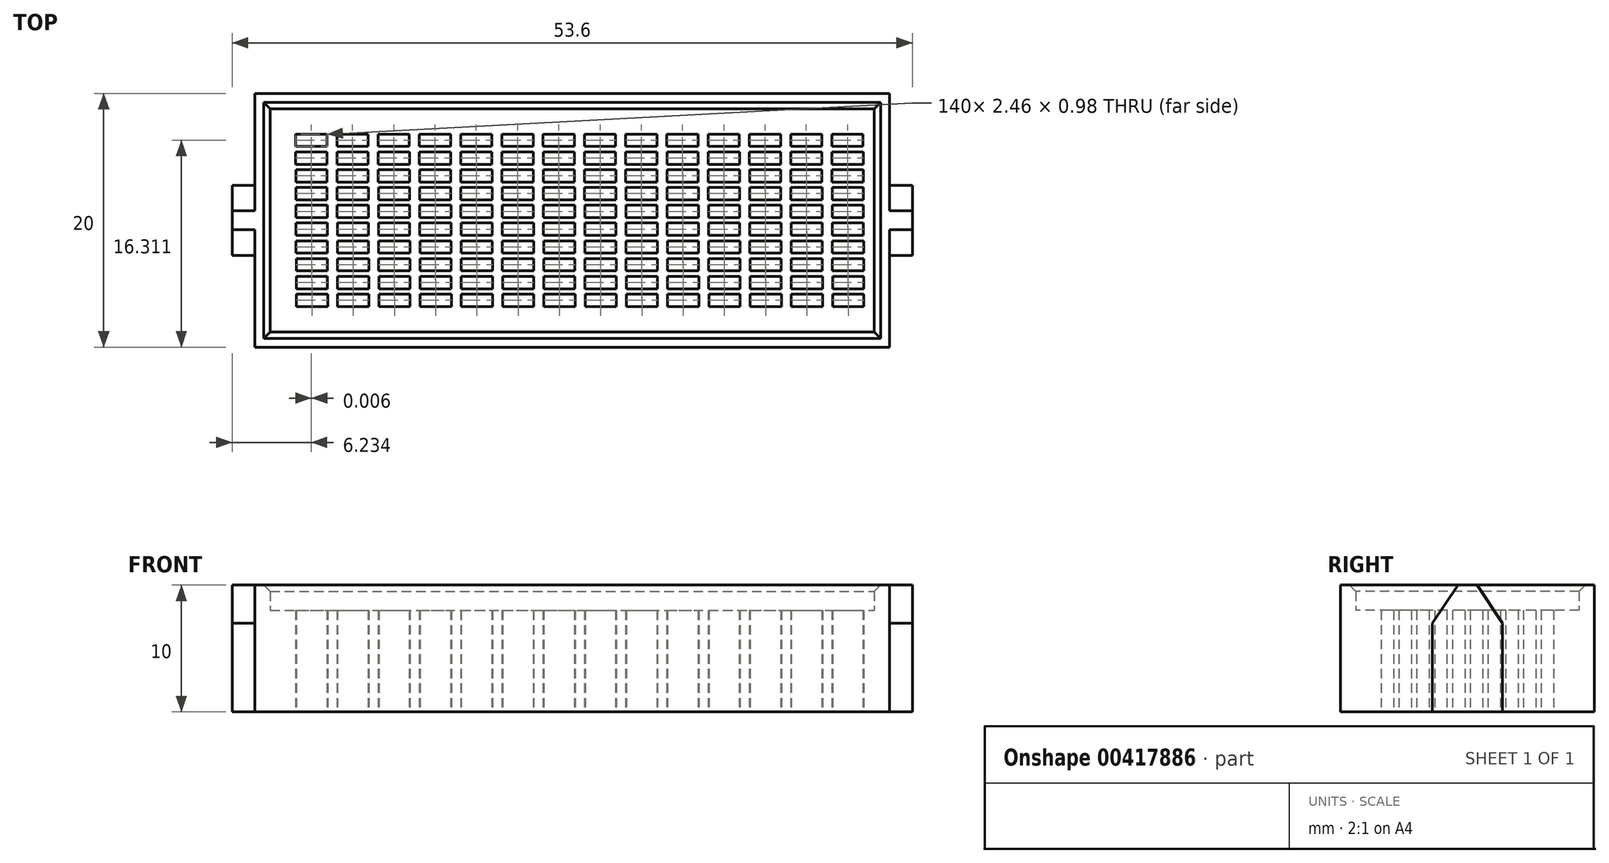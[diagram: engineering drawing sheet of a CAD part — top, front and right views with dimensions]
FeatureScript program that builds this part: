
annotation { "Feature Type Name" : "Feature", "Feature Type Description" : "" }
export const myFeature = defineFeature(function(context is Context, id is Id, definition is map)
    precondition{}
    {
        {
            var Q0;
            Q0=qCreatedBy(makeId("Top.planeOp"),FACE);
            var sketch = newSketch(context, id + "F0", { "sketchPlane" : qUnion([Q0])});
            skLineSegment(sketch, "E0.bottom", {"start": v(-104.56, 20) * mm, "end": v(-54.56, 20) * mm});
            skLineSegment(sketch, "E0.top", {"start": v(-104.56, 0) * mm, "end": v(-54.56, 0) * mm});
            skLineSegment(sketch, "E0.left", {"start": v(-104.56, 20) * mm, "end": v(-104.56, 0) * mm});
            skLineSegment(sketch, "E0.right", {"start": v(-54.56, 20) * mm, "end": v(-54.56, 0) * mm});
            skLineSegment(sketch, "E1.0", {"start": v(-103.36, 1.2) * mm, "end": v(-55.76, 1.2) * mm});
            skLineSegment(sketch, "E1.1", {"start": v(-103.36, 18.8) * mm, "end": v(-103.36, 1.2) * mm});
            skLineSegment(sketch, "E1.2", {"start": v(-103.36, 18.8) * mm, "end": v(-55.76, 18.8) * mm});
            skLineSegment(sketch, "E1.3", {"start": v(-55.76, 18.8) * mm, "end": v(-55.76, 1.2) * mm});
            skLineSegment(sketch, "E2.bottom", {"start": v(-101.36, 16.8) * mm, "end": v(-98.9, 16.8) * mm});
            skLineSegment(sketch, "E2.top", {"start": v(-101.36, 15.82) * mm, "end": v(-98.9, 15.82) * mm});
            skLineSegment(sketch, "E2.left", {"start": v(-101.36, 16.8) * mm, "end": v(-101.36, 15.82) * mm});
            skLineSegment(sketch, "E2.right", {"start": v(-98.9, 16.8) * mm, "end": v(-98.9, 15.82) * mm});
            skLineSegment(sketch, "E3.1.0.0", {"start": v(-98.1, 15.82) * mm, "end": v(-95.65, 15.82) * mm});
            skLineSegment(sketch, "E3.1.0.1", {"start": v(-98.1, 16.8) * mm, "end": v(-95.65, 16.8) * mm});
            skLineSegment(sketch, "E3.1.0.2", {"start": v(-98.1, 16.8) * mm, "end": v(-98.1, 15.82) * mm});
            skLineSegment(sketch, "E3.1.0.3", {"start": v(-95.65, 16.8) * mm, "end": v(-95.65, 15.82) * mm});
            skLineSegment(sketch, "E3.2.0.0", {"start": v(-94.86, 15.82) * mm, "end": v(-92.4, 15.82) * mm});
            skLineSegment(sketch, "E3.2.0.1", {"start": v(-94.86, 16.8) * mm, "end": v(-92.4, 16.8) * mm});
            skLineSegment(sketch, "E3.2.0.2", {"start": v(-94.86, 16.8) * mm, "end": v(-94.86, 15.82) * mm});
            skLineSegment(sketch, "E3.2.0.3", {"start": v(-92.4, 16.8) * mm, "end": v(-92.4, 15.82) * mm});
            skLineSegment(sketch, "E3.3.0.0", {"start": v(-91.6, 15.82) * mm, "end": v(-89.15, 15.82) * mm});
            skLineSegment(sketch, "E3.3.0.1", {"start": v(-91.6, 16.8) * mm, "end": v(-89.15, 16.8) * mm});
            skLineSegment(sketch, "E3.3.0.2", {"start": v(-91.6, 16.8) * mm, "end": v(-91.6, 15.82) * mm});
            skLineSegment(sketch, "E3.3.0.3", {"start": v(-89.15, 16.8) * mm, "end": v(-89.15, 15.82) * mm});
            skLineSegment(sketch, "E3.4.0.0", {"start": v(-88.36, 15.82) * mm, "end": v(-85.9, 15.82) * mm});
            skLineSegment(sketch, "E3.4.0.1", {"start": v(-88.36, 16.8) * mm, "end": v(-85.9, 16.8) * mm});
            skLineSegment(sketch, "E3.4.0.2", {"start": v(-88.36, 16.8) * mm, "end": v(-88.36, 15.82) * mm});
            skLineSegment(sketch, "E3.4.0.3", {"start": v(-85.9, 16.8) * mm, "end": v(-85.9, 15.82) * mm});
            skLineSegment(sketch, "E3.5.0.0", {"start": v(-85.1, 15.82) * mm, "end": v(-82.65, 15.82) * mm});
            skLineSegment(sketch, "E3.5.0.1", {"start": v(-85.1, 16.8) * mm, "end": v(-82.65, 16.8) * mm});
            skLineSegment(sketch, "E3.5.0.2", {"start": v(-85.1, 16.8) * mm, "end": v(-85.1, 15.82) * mm});
            skLineSegment(sketch, "E3.5.0.3", {"start": v(-82.65, 16.8) * mm, "end": v(-82.65, 15.82) * mm});
            skLineSegment(sketch, "E3.6.0.0", {"start": v(-81.86, 15.82) * mm, "end": v(-79.4, 15.82) * mm});
            skLineSegment(sketch, "E3.6.0.1", {"start": v(-81.86, 16.8) * mm, "end": v(-79.4, 16.8) * mm});
            skLineSegment(sketch, "E3.6.0.2", {"start": v(-81.86, 16.8) * mm, "end": v(-81.86, 15.82) * mm});
            skLineSegment(sketch, "E3.6.0.3", {"start": v(-79.4, 16.8) * mm, "end": v(-79.4, 15.82) * mm});
            skLineSegment(sketch, "E3.7.0.0", {"start": v(-78.6, 15.82) * mm, "end": v(-76.15, 15.82) * mm});
            skLineSegment(sketch, "E3.7.0.1", {"start": v(-78.6, 16.8) * mm, "end": v(-76.15, 16.8) * mm});
            skLineSegment(sketch, "E3.7.0.2", {"start": v(-78.6, 16.8) * mm, "end": v(-78.6, 15.82) * mm});
            skLineSegment(sketch, "E3.7.0.3", {"start": v(-76.15, 16.8) * mm, "end": v(-76.15, 15.82) * mm});
            skLineSegment(sketch, "E3.8.0.0", {"start": v(-75.36, 15.82) * mm, "end": v(-72.9, 15.82) * mm});
            skLineSegment(sketch, "E3.8.0.1", {"start": v(-75.36, 16.8) * mm, "end": v(-72.9, 16.8) * mm});
            skLineSegment(sketch, "E3.8.0.2", {"start": v(-75.36, 16.8) * mm, "end": v(-75.36, 15.82) * mm});
            skLineSegment(sketch, "E3.8.0.3", {"start": v(-72.9, 16.8) * mm, "end": v(-72.9, 15.82) * mm});
            skLineSegment(sketch, "E3.9.0.0", {"start": v(-72.1, 15.82) * mm, "end": v(-69.65, 15.82) * mm});
            skLineSegment(sketch, "E3.9.0.1", {"start": v(-72.1, 16.8) * mm, "end": v(-69.65, 16.8) * mm});
            skLineSegment(sketch, "E3.9.0.2", {"start": v(-72.1, 16.8) * mm, "end": v(-72.1, 15.82) * mm});
            skLineSegment(sketch, "E3.9.0.3", {"start": v(-69.65, 16.8) * mm, "end": v(-69.65, 15.82) * mm});
            skLineSegment(sketch, "E3.10.0.0", {"start": v(-68.86, 15.82) * mm, "end": v(-66.4, 15.82) * mm});
            skLineSegment(sketch, "E3.10.0.1", {"start": v(-68.86, 16.8) * mm, "end": v(-66.4, 16.8) * mm});
            skLineSegment(sketch, "E3.10.0.2", {"start": v(-68.86, 16.8) * mm, "end": v(-68.86, 15.82) * mm});
            skLineSegment(sketch, "E3.10.0.3", {"start": v(-66.4, 16.8) * mm, "end": v(-66.4, 15.82) * mm});
            skLineSegment(sketch, "E3.11.0.0", {"start": v(-65.6, 15.82) * mm, "end": v(-63.15, 15.82) * mm});
            skLineSegment(sketch, "E3.11.0.1", {"start": v(-65.6, 16.8) * mm, "end": v(-63.15, 16.8) * mm});
            skLineSegment(sketch, "E3.11.0.2", {"start": v(-65.6, 16.8) * mm, "end": v(-65.6, 15.82) * mm});
            skLineSegment(sketch, "E3.11.0.3", {"start": v(-63.15, 16.8) * mm, "end": v(-63.15, 15.82) * mm});
            skLineSegment(sketch, "E3.12.0.0", {"start": v(-62.36, 15.82) * mm, "end": v(-59.9, 15.82) * mm});
            skLineSegment(sketch, "E3.12.0.1", {"start": v(-62.36, 16.8) * mm, "end": v(-59.9, 16.8) * mm});
            skLineSegment(sketch, "E3.12.0.2", {"start": v(-62.36, 16.8) * mm, "end": v(-62.36, 15.82) * mm});
            skLineSegment(sketch, "E3.12.0.3", {"start": v(-59.9, 16.8) * mm, "end": v(-59.9, 15.82) * mm});
            skLineSegment(sketch, "E3.13.0.0", {"start": v(-59.1, 15.82) * mm, "end": v(-56.65, 15.82) * mm});
            skLineSegment(sketch, "E3.13.0.1", {"start": v(-59.1, 16.8) * mm, "end": v(-56.65, 16.8) * mm});
            skLineSegment(sketch, "E3.13.0.2", {"start": v(-59.1, 16.8) * mm, "end": v(-59.1, 15.82) * mm});
            skLineSegment(sketch, "E3.13.0.3", {"start": v(-56.65, 16.8) * mm, "end": v(-56.65, 15.82) * mm});
            skLineSegment(sketch, "E3.direction1", {"start": v(-101.36, 15.82) * mm, "end": v(-98.1, 15.82) * mm, "construction": true});
            skLineSegment(sketch, "E4.1.0.1", {"start": v(-88.35, 14.42) * mm, "end": v(-85.89, 14.42) * mm});
            skLineSegment(sketch, "E4.1.0.2", {"start": v(-81.85, 15.4) * mm, "end": v(-79.39, 15.4) * mm});
            skLineSegment(sketch, "E4.1.0.3", {"start": v(-62.35, 15.4) * mm, "end": v(-59.89, 15.4) * mm});
            skLineSegment(sketch, "E4.1.0.4", {"start": v(-62.35, 14.42) * mm, "end": v(-59.89, 14.42) * mm});
            skLineSegment(sketch, "E4.1.0.5", {"start": v(-68.85, 15.4) * mm, "end": v(-66.39, 15.4) * mm});
            skLineSegment(sketch, "E4.1.0.7", {"start": v(-88.35, 15.4) * mm, "end": v(-85.89, 15.4) * mm});
            skLineSegment(sketch, "E4.1.0.8", {"start": v(-75.35, 15.4) * mm, "end": v(-72.89, 15.4) * mm});
            skLineSegment(sketch, "E4.1.0.10", {"start": v(-94.85, 15.4) * mm, "end": v(-92.39, 15.4) * mm});
            skLineSegment(sketch, "E4.1.0.12", {"start": v(-75.35, 14.42) * mm, "end": v(-72.89, 14.42) * mm});
            skLineSegment(sketch, "E4.1.0.14", {"start": v(-59.1, 14.42) * mm, "end": v(-56.64, 14.42) * mm});
            skLineSegment(sketch, "E4.1.0.15", {"start": v(-72.1, 14.42) * mm, "end": v(-69.64, 14.42) * mm});
            skLineSegment(sketch, "E4.1.0.16", {"start": v(-85.1, 14.42) * mm, "end": v(-82.64, 14.42) * mm});
            skLineSegment(sketch, "E4.1.0.17", {"start": v(-91.6, 14.42) * mm, "end": v(-89.14, 14.42) * mm});
            skLineSegment(sketch, "E4.1.0.19", {"start": v(-59.1, 15.4) * mm, "end": v(-56.64, 15.4) * mm});
            skLineSegment(sketch, "E4.1.0.21", {"start": v(-72.1, 15.4) * mm, "end": v(-69.64, 15.4) * mm});
            skLineSegment(sketch, "E4.1.0.22", {"start": v(-65.6, 14.42) * mm, "end": v(-63.14, 14.42) * mm});
            skLineSegment(sketch, "E4.1.0.23", {"start": v(-85.1, 15.4) * mm, "end": v(-82.64, 15.4) * mm});
            skLineSegment(sketch, "E4.1.0.24", {"start": v(-78.6, 14.42) * mm, "end": v(-76.14, 14.42) * mm});
            skLineSegment(sketch, "E4.1.0.25", {"start": v(-98.1, 14.42) * mm, "end": v(-95.64, 14.42) * mm});
            skLineSegment(sketch, "E4.1.0.26", {"start": v(-98.1, 15.4) * mm, "end": v(-95.64, 15.4) * mm});
            skLineSegment(sketch, "E4.1.0.27", {"start": v(-101.35, 15.4) * mm, "end": v(-98.89, 15.4) * mm});
            skLineSegment(sketch, "E4.1.0.28", {"start": v(-65.6, 15.4) * mm, "end": v(-63.14, 15.4) * mm});
            skLineSegment(sketch, "E4.1.0.29", {"start": v(-78.6, 15.4) * mm, "end": v(-76.14, 15.4) * mm});
            skLineSegment(sketch, "E4.1.0.30", {"start": v(-91.6, 15.4) * mm, "end": v(-89.14, 15.4) * mm});
            skLineSegment(sketch, "E4.1.0.32", {"start": v(-94.85, 14.42) * mm, "end": v(-92.39, 14.42) * mm});
            skLineSegment(sketch, "E4.1.0.33", {"start": v(-101.35, 14.42) * mm, "end": v(-98.1, 14.42) * mm, "construction": true});
            skLineSegment(sketch, "E4.1.0.35", {"start": v(-68.85, 14.42) * mm, "end": v(-66.39, 14.42) * mm});
            skLineSegment(sketch, "E4.1.0.36", {"start": v(-81.85, 14.42) * mm, "end": v(-79.39, 14.42) * mm});
            skLineSegment(sketch, "E4.1.0.37", {"start": v(-101.35, 14.42) * mm, "end": v(-98.89, 14.42) * mm});
            skLineSegment(sketch, "E4.1.0.38", {"start": v(-94.85, 15.4) * mm, "end": v(-94.85, 14.42) * mm});
            skLineSegment(sketch, "E4.1.0.41", {"start": v(-59.89, 15.4) * mm, "end": v(-59.89, 14.42) * mm});
            skLineSegment(sketch, "E4.1.0.42", {"start": v(-72.89, 15.4) * mm, "end": v(-72.89, 14.42) * mm});
            skLineSegment(sketch, "E4.1.0.43", {"start": v(-68.85, 15.4) * mm, "end": v(-68.85, 14.42) * mm});
            skLineSegment(sketch, "E4.1.0.44", {"start": v(-85.89, 15.4) * mm, "end": v(-85.89, 14.42) * mm});
            skLineSegment(sketch, "E4.1.0.45", {"start": v(-81.85, 15.4) * mm, "end": v(-81.85, 14.42) * mm});
            skLineSegment(sketch, "E4.1.0.46", {"start": v(-62.35, 15.4) * mm, "end": v(-62.35, 14.42) * mm});
            skLineSegment(sketch, "E4.1.0.47", {"start": v(-75.35, 15.4) * mm, "end": v(-75.35, 14.42) * mm});
            skLineSegment(sketch, "E4.1.0.48", {"start": v(-88.35, 15.4) * mm, "end": v(-88.35, 14.42) * mm});
            skLineSegment(sketch, "E4.1.0.50", {"start": v(-92.39, 15.4) * mm, "end": v(-92.39, 14.42) * mm});
            skLineSegment(sketch, "E4.1.0.52", {"start": v(-66.39, 15.4) * mm, "end": v(-66.39, 14.42) * mm});
            skLineSegment(sketch, "E4.1.0.53", {"start": v(-79.39, 15.4) * mm, "end": v(-79.39, 14.42) * mm});
            skLineSegment(sketch, "E4.1.0.54", {"start": v(-98.89, 15.4) * mm, "end": v(-98.89, 14.42) * mm});
            skLineSegment(sketch, "E4.1.0.55", {"start": v(-101.35, 15.4) * mm, "end": v(-101.35, 14.42) * mm});
            skLineSegment(sketch, "E4.1.0.56", {"start": v(-98.1, 15.4) * mm, "end": v(-98.1, 14.42) * mm});
            skLineSegment(sketch, "E4.1.0.58", {"start": v(-59.1, 15.4) * mm, "end": v(-59.1, 14.42) * mm});
            skLineSegment(sketch, "E4.1.0.59", {"start": v(-72.1, 15.4) * mm, "end": v(-72.1, 14.42) * mm});
            skLineSegment(sketch, "E4.1.0.60", {"start": v(-85.1, 15.4) * mm, "end": v(-85.1, 14.42) * mm});
            skLineSegment(sketch, "E4.1.0.61", {"start": v(-65.6, 15.4) * mm, "end": v(-65.6, 14.42) * mm});
            skLineSegment(sketch, "E4.1.0.62", {"start": v(-78.6, 15.4) * mm, "end": v(-78.6, 14.42) * mm});
            skLineSegment(sketch, "E4.1.0.63", {"start": v(-91.6, 15.4) * mm, "end": v(-91.6, 14.42) * mm});
            skLineSegment(sketch, "E4.1.0.65", {"start": v(-95.64, 15.4) * mm, "end": v(-95.64, 14.42) * mm});
            skLineSegment(sketch, "E4.1.0.67", {"start": v(-56.64, 15.4) * mm, "end": v(-56.64, 14.42) * mm});
            skLineSegment(sketch, "E4.1.0.68", {"start": v(-69.64, 15.4) * mm, "end": v(-69.64, 14.42) * mm});
            skLineSegment(sketch, "E4.1.0.69", {"start": v(-82.64, 15.4) * mm, "end": v(-82.64, 14.42) * mm});
            skLineSegment(sketch, "E4.1.0.70", {"start": v(-63.14, 15.4) * mm, "end": v(-63.14, 14.42) * mm});
            skLineSegment(sketch, "E4.1.0.71", {"start": v(-76.14, 15.4) * mm, "end": v(-76.14, 14.42) * mm});
            skLineSegment(sketch, "E4.1.0.72", {"start": v(-89.14, 15.4) * mm, "end": v(-89.14, 14.42) * mm});
            skLineSegment(sketch, "E4.2.0.1", {"start": v(-88.34, 13.02) * mm, "end": v(-85.88, 13.02) * mm});
            skLineSegment(sketch, "E4.2.0.2", {"start": v(-81.84, 14) * mm, "end": v(-79.38, 14) * mm});
            skLineSegment(sketch, "E4.2.0.3", {"start": v(-62.34, 14) * mm, "end": v(-59.88, 14) * mm});
            skLineSegment(sketch, "E4.2.0.4", {"start": v(-62.34, 13.02) * mm, "end": v(-59.88, 13.02) * mm});
            skLineSegment(sketch, "E4.2.0.5", {"start": v(-68.84, 14) * mm, "end": v(-66.38, 14) * mm});
            skLineSegment(sketch, "E4.2.0.7", {"start": v(-88.34, 14) * mm, "end": v(-85.88, 14) * mm});
            skLineSegment(sketch, "E4.2.0.8", {"start": v(-75.34, 14) * mm, "end": v(-72.88, 14) * mm});
            skLineSegment(sketch, "E4.2.0.10", {"start": v(-94.84, 14) * mm, "end": v(-92.38, 14) * mm});
            skLineSegment(sketch, "E4.2.0.12", {"start": v(-75.34, 13.02) * mm, "end": v(-72.88, 13.02) * mm});
            skLineSegment(sketch, "E4.2.0.14", {"start": v(-59.1, 13.02) * mm, "end": v(-56.63, 13.02) * mm});
            skLineSegment(sketch, "E4.2.0.15", {"start": v(-72.1, 13.02) * mm, "end": v(-69.63, 13.02) * mm});
            skLineSegment(sketch, "E4.2.0.16", {"start": v(-85.1, 13.02) * mm, "end": v(-82.63, 13.02) * mm});
            skLineSegment(sketch, "E4.2.0.17", {"start": v(-91.6, 13.02) * mm, "end": v(-89.13, 13.02) * mm});
            skLineSegment(sketch, "E4.2.0.19", {"start": v(-59.1, 14) * mm, "end": v(-56.63, 14) * mm});
            skLineSegment(sketch, "E4.2.0.21", {"start": v(-72.1, 14) * mm, "end": v(-69.63, 14) * mm});
            skLineSegment(sketch, "E4.2.0.22", {"start": v(-65.6, 13.02) * mm, "end": v(-63.13, 13.02) * mm});
            skLineSegment(sketch, "E4.2.0.23", {"start": v(-85.1, 14) * mm, "end": v(-82.63, 14) * mm});
            skLineSegment(sketch, "E4.2.0.24", {"start": v(-78.6, 13.02) * mm, "end": v(-76.13, 13.02) * mm});
            skLineSegment(sketch, "E4.2.0.25", {"start": v(-98.1, 13.02) * mm, "end": v(-95.63, 13.02) * mm});
            skLineSegment(sketch, "E4.2.0.26", {"start": v(-98.1, 14) * mm, "end": v(-95.63, 14) * mm});
            skLineSegment(sketch, "E4.2.0.27", {"start": v(-101.34, 14) * mm, "end": v(-98.88, 14) * mm});
            skLineSegment(sketch, "E4.2.0.28", {"start": v(-65.6, 14) * mm, "end": v(-63.13, 14) * mm});
            skLineSegment(sketch, "E4.2.0.29", {"start": v(-78.6, 14) * mm, "end": v(-76.13, 14) * mm});
            skLineSegment(sketch, "E4.2.0.30", {"start": v(-91.6, 14) * mm, "end": v(-89.13, 14) * mm});
            skLineSegment(sketch, "E4.2.0.32", {"start": v(-94.84, 13.02) * mm, "end": v(-92.38, 13.02) * mm});
            skLineSegment(sketch, "E4.2.0.33", {"start": v(-101.34, 13.02) * mm, "end": v(-98.1, 13.02) * mm, "construction": true});
            skLineSegment(sketch, "E4.2.0.35", {"start": v(-68.84, 13.02) * mm, "end": v(-66.38, 13.02) * mm});
            skLineSegment(sketch, "E4.2.0.36", {"start": v(-81.84, 13.02) * mm, "end": v(-79.38, 13.02) * mm});
            skLineSegment(sketch, "E4.2.0.37", {"start": v(-101.34, 13.02) * mm, "end": v(-98.88, 13.02) * mm});
            skLineSegment(sketch, "E4.2.0.38", {"start": v(-94.84, 14) * mm, "end": v(-94.84, 13.02) * mm});
            skLineSegment(sketch, "E4.2.0.41", {"start": v(-59.88, 14) * mm, "end": v(-59.88, 13.02) * mm});
            skLineSegment(sketch, "E4.2.0.42", {"start": v(-72.88, 14) * mm, "end": v(-72.88, 13.02) * mm});
            skLineSegment(sketch, "E4.2.0.43", {"start": v(-68.84, 14) * mm, "end": v(-68.84, 13.02) * mm});
            skLineSegment(sketch, "E4.2.0.44", {"start": v(-85.88, 14) * mm, "end": v(-85.88, 13.02) * mm});
            skLineSegment(sketch, "E4.2.0.45", {"start": v(-81.84, 14) * mm, "end": v(-81.84, 13.02) * mm});
            skLineSegment(sketch, "E4.2.0.46", {"start": v(-62.34, 14) * mm, "end": v(-62.34, 13.02) * mm});
            skLineSegment(sketch, "E4.2.0.47", {"start": v(-75.34, 14) * mm, "end": v(-75.34, 13.02) * mm});
            skLineSegment(sketch, "E4.2.0.48", {"start": v(-88.34, 14) * mm, "end": v(-88.34, 13.02) * mm});
            skLineSegment(sketch, "E4.2.0.50", {"start": v(-92.38, 14) * mm, "end": v(-92.38, 13.02) * mm});
            skLineSegment(sketch, "E4.2.0.52", {"start": v(-66.38, 14) * mm, "end": v(-66.38, 13.02) * mm});
            skLineSegment(sketch, "E4.2.0.53", {"start": v(-79.38, 14) * mm, "end": v(-79.38, 13.02) * mm});
            skLineSegment(sketch, "E4.2.0.54", {"start": v(-98.88, 14) * mm, "end": v(-98.88, 13.02) * mm});
            skLineSegment(sketch, "E4.2.0.55", {"start": v(-101.34, 14) * mm, "end": v(-101.34, 13.02) * mm});
            skLineSegment(sketch, "E4.2.0.56", {"start": v(-98.1, 14) * mm, "end": v(-98.1, 13.02) * mm});
            skLineSegment(sketch, "E4.2.0.58", {"start": v(-59.1, 14) * mm, "end": v(-59.1, 13.02) * mm});
            skLineSegment(sketch, "E4.2.0.59", {"start": v(-72.1, 14) * mm, "end": v(-72.1, 13.02) * mm});
            skLineSegment(sketch, "E4.2.0.60", {"start": v(-85.1, 14) * mm, "end": v(-85.1, 13.02) * mm});
            skLineSegment(sketch, "E4.2.0.61", {"start": v(-65.6, 14) * mm, "end": v(-65.6, 13.02) * mm});
            skLineSegment(sketch, "E4.2.0.62", {"start": v(-78.6, 14) * mm, "end": v(-78.6, 13.02) * mm});
            skLineSegment(sketch, "E4.2.0.63", {"start": v(-91.6, 14) * mm, "end": v(-91.6, 13.02) * mm});
            skLineSegment(sketch, "E4.2.0.65", {"start": v(-95.63, 14) * mm, "end": v(-95.63, 13.02) * mm});
            skLineSegment(sketch, "E4.2.0.67", {"start": v(-56.63, 14) * mm, "end": v(-56.63, 13.02) * mm});
            skLineSegment(sketch, "E4.2.0.68", {"start": v(-69.63, 14) * mm, "end": v(-69.63, 13.02) * mm});
            skLineSegment(sketch, "E4.2.0.69", {"start": v(-82.63, 14) * mm, "end": v(-82.63, 13.02) * mm});
            skLineSegment(sketch, "E4.2.0.70", {"start": v(-63.13, 14) * mm, "end": v(-63.13, 13.02) * mm});
            skLineSegment(sketch, "E4.2.0.71", {"start": v(-76.13, 14) * mm, "end": v(-76.13, 13.02) * mm});
            skLineSegment(sketch, "E4.2.0.72", {"start": v(-89.13, 14) * mm, "end": v(-89.13, 13.02) * mm});
            skLineSegment(sketch, "E4.3.0.1", {"start": v(-88.34, 11.62) * mm, "end": v(-85.88, 11.62) * mm});
            skLineSegment(sketch, "E4.3.0.2", {"start": v(-81.84, 12.6) * mm, "end": v(-79.38, 12.6) * mm});
            skLineSegment(sketch, "E4.3.0.3", {"start": v(-62.34, 12.6) * mm, "end": v(-59.88, 12.6) * mm});
            skLineSegment(sketch, "E4.3.0.4", {"start": v(-62.34, 11.62) * mm, "end": v(-59.88, 11.62) * mm});
            skLineSegment(sketch, "E4.3.0.5", {"start": v(-68.84, 12.6) * mm, "end": v(-66.38, 12.6) * mm});
            skLineSegment(sketch, "E4.3.0.7", {"start": v(-88.34, 12.6) * mm, "end": v(-85.88, 12.6) * mm});
            skLineSegment(sketch, "E4.3.0.8", {"start": v(-75.34, 12.6) * mm, "end": v(-72.88, 12.6) * mm});
            skLineSegment(sketch, "E4.3.0.10", {"start": v(-94.84, 12.6) * mm, "end": v(-92.38, 12.6) * mm});
            skLineSegment(sketch, "E4.3.0.12", {"start": v(-75.34, 11.62) * mm, "end": v(-72.88, 11.62) * mm});
            skLineSegment(sketch, "E4.3.0.14", {"start": v(-59.09, 11.62) * mm, "end": v(-56.63, 11.62) * mm});
            skLineSegment(sketch, "E4.3.0.15", {"start": v(-72.09, 11.62) * mm, "end": v(-69.63, 11.62) * mm});
            skLineSegment(sketch, "E4.3.0.16", {"start": v(-85.09, 11.62) * mm, "end": v(-82.63, 11.62) * mm});
            skLineSegment(sketch, "E4.3.0.17", {"start": v(-91.59, 11.62) * mm, "end": v(-89.13, 11.62) * mm});
            skLineSegment(sketch, "E4.3.0.19", {"start": v(-59.09, 12.6) * mm, "end": v(-56.63, 12.6) * mm});
            skLineSegment(sketch, "E4.3.0.21", {"start": v(-72.09, 12.6) * mm, "end": v(-69.63, 12.6) * mm});
            skLineSegment(sketch, "E4.3.0.22", {"start": v(-65.59, 11.62) * mm, "end": v(-63.13, 11.62) * mm});
            skLineSegment(sketch, "E4.3.0.23", {"start": v(-85.09, 12.6) * mm, "end": v(-82.63, 12.6) * mm});
            skLineSegment(sketch, "E4.3.0.24", {"start": v(-78.59, 11.62) * mm, "end": v(-76.13, 11.62) * mm});
            skLineSegment(sketch, "E4.3.0.25", {"start": v(-98.09, 11.62) * mm, "end": v(-95.63, 11.62) * mm});
            skLineSegment(sketch, "E4.3.0.26", {"start": v(-98.09, 12.6) * mm, "end": v(-95.63, 12.6) * mm});
            skLineSegment(sketch, "E4.3.0.27", {"start": v(-101.34, 12.6) * mm, "end": v(-98.88, 12.6) * mm});
            skLineSegment(sketch, "E4.3.0.28", {"start": v(-65.59, 12.6) * mm, "end": v(-63.13, 12.6) * mm});
            skLineSegment(sketch, "E4.3.0.29", {"start": v(-78.59, 12.6) * mm, "end": v(-76.13, 12.6) * mm});
            skLineSegment(sketch, "E4.3.0.30", {"start": v(-91.59, 12.6) * mm, "end": v(-89.13, 12.6) * mm});
            skLineSegment(sketch, "E4.3.0.32", {"start": v(-94.84, 11.62) * mm, "end": v(-92.38, 11.62) * mm});
            skLineSegment(sketch, "E4.3.0.33", {"start": v(-101.34, 11.62) * mm, "end": v(-98.09, 11.62) * mm, "construction": true});
            skLineSegment(sketch, "E4.3.0.35", {"start": v(-68.84, 11.62) * mm, "end": v(-66.38, 11.62) * mm});
            skLineSegment(sketch, "E4.3.0.36", {"start": v(-81.84, 11.62) * mm, "end": v(-79.38, 11.62) * mm});
            skLineSegment(sketch, "E4.3.0.37", {"start": v(-101.34, 11.62) * mm, "end": v(-98.88, 11.62) * mm});
            skLineSegment(sketch, "E4.3.0.38", {"start": v(-94.84, 12.6) * mm, "end": v(-94.84, 11.62) * mm});
            skLineSegment(sketch, "E4.3.0.41", {"start": v(-59.88, 12.6) * mm, "end": v(-59.88, 11.62) * mm});
            skLineSegment(sketch, "E4.3.0.42", {"start": v(-72.88, 12.6) * mm, "end": v(-72.88, 11.62) * mm});
            skLineSegment(sketch, "E4.3.0.43", {"start": v(-68.84, 12.6) * mm, "end": v(-68.84, 11.62) * mm});
            skLineSegment(sketch, "E4.3.0.44", {"start": v(-85.88, 12.6) * mm, "end": v(-85.88, 11.62) * mm});
            skLineSegment(sketch, "E4.3.0.45", {"start": v(-81.84, 12.6) * mm, "end": v(-81.84, 11.62) * mm});
            skLineSegment(sketch, "E4.3.0.46", {"start": v(-62.34, 12.6) * mm, "end": v(-62.34, 11.62) * mm});
            skLineSegment(sketch, "E4.3.0.47", {"start": v(-75.34, 12.6) * mm, "end": v(-75.34, 11.62) * mm});
            skLineSegment(sketch, "E4.3.0.48", {"start": v(-88.34, 12.6) * mm, "end": v(-88.34, 11.62) * mm});
            skLineSegment(sketch, "E4.3.0.50", {"start": v(-92.38, 12.6) * mm, "end": v(-92.38, 11.62) * mm});
            skLineSegment(sketch, "E4.3.0.52", {"start": v(-66.38, 12.6) * mm, "end": v(-66.38, 11.62) * mm});
            skLineSegment(sketch, "E4.3.0.53", {"start": v(-79.38, 12.6) * mm, "end": v(-79.38, 11.62) * mm});
            skLineSegment(sketch, "E4.3.0.54", {"start": v(-98.88, 12.6) * mm, "end": v(-98.88, 11.62) * mm});
            skLineSegment(sketch, "E4.3.0.55", {"start": v(-101.34, 12.6) * mm, "end": v(-101.34, 11.62) * mm});
            skLineSegment(sketch, "E4.3.0.56", {"start": v(-98.09, 12.6) * mm, "end": v(-98.09, 11.62) * mm});
            skLineSegment(sketch, "E4.3.0.58", {"start": v(-59.09, 12.6) * mm, "end": v(-59.09, 11.62) * mm});
            skLineSegment(sketch, "E4.3.0.59", {"start": v(-72.09, 12.6) * mm, "end": v(-72.09, 11.62) * mm});
            skLineSegment(sketch, "E4.3.0.60", {"start": v(-85.09, 12.6) * mm, "end": v(-85.09, 11.62) * mm});
            skLineSegment(sketch, "E4.3.0.61", {"start": v(-65.59, 12.6) * mm, "end": v(-65.59, 11.62) * mm});
            skLineSegment(sketch, "E4.3.0.62", {"start": v(-78.59, 12.6) * mm, "end": v(-78.59, 11.62) * mm});
            skLineSegment(sketch, "E4.3.0.63", {"start": v(-91.59, 12.6) * mm, "end": v(-91.59, 11.62) * mm});
            skLineSegment(sketch, "E4.3.0.65", {"start": v(-95.63, 12.6) * mm, "end": v(-95.63, 11.62) * mm});
            skLineSegment(sketch, "E4.3.0.67", {"start": v(-56.63, 12.6) * mm, "end": v(-56.63, 11.62) * mm});
            skLineSegment(sketch, "E4.3.0.68", {"start": v(-69.63, 12.6) * mm, "end": v(-69.63, 11.62) * mm});
            skLineSegment(sketch, "E4.3.0.69", {"start": v(-82.63, 12.6) * mm, "end": v(-82.63, 11.62) * mm});
            skLineSegment(sketch, "E4.3.0.70", {"start": v(-63.13, 12.6) * mm, "end": v(-63.13, 11.62) * mm});
            skLineSegment(sketch, "E4.3.0.71", {"start": v(-76.13, 12.6) * mm, "end": v(-76.13, 11.62) * mm});
            skLineSegment(sketch, "E4.3.0.72", {"start": v(-89.13, 12.6) * mm, "end": v(-89.13, 11.62) * mm});
            skLineSegment(sketch, "E4.4.0.1", {"start": v(-88.33, 10.21) * mm, "end": v(-85.87, 10.21) * mm});
            skLineSegment(sketch, "E4.4.0.2", {"start": v(-81.83, 11.2) * mm, "end": v(-79.37, 11.2) * mm});
            skLineSegment(sketch, "E4.4.0.3", {"start": v(-62.33, 11.2) * mm, "end": v(-59.87, 11.2) * mm});
            skLineSegment(sketch, "E4.4.0.4", {"start": v(-62.33, 10.21) * mm, "end": v(-59.87, 10.21) * mm});
            skLineSegment(sketch, "E4.4.0.5", {"start": v(-68.83, 11.2) * mm, "end": v(-66.37, 11.2) * mm});
            skLineSegment(sketch, "E4.4.0.7", {"start": v(-88.33, 11.2) * mm, "end": v(-85.87, 11.2) * mm});
            skLineSegment(sketch, "E4.4.0.8", {"start": v(-75.33, 11.2) * mm, "end": v(-72.87, 11.2) * mm});
            skLineSegment(sketch, "E4.4.0.10", {"start": v(-94.83, 11.2) * mm, "end": v(-92.37, 11.2) * mm});
            skLineSegment(sketch, "E4.4.0.12", {"start": v(-75.33, 10.21) * mm, "end": v(-72.87, 10.21) * mm});
            skLineSegment(sketch, "E4.4.0.14", {"start": v(-59.08, 10.21) * mm, "end": v(-56.62, 10.21) * mm});
            skLineSegment(sketch, "E4.4.0.15", {"start": v(-72.08, 10.21) * mm, "end": v(-69.62, 10.21) * mm});
            skLineSegment(sketch, "E4.4.0.16", {"start": v(-85.08, 10.21) * mm, "end": v(-82.62, 10.21) * mm});
            skLineSegment(sketch, "E4.4.0.17", {"start": v(-91.58, 10.21) * mm, "end": v(-89.12, 10.21) * mm});
            skLineSegment(sketch, "E4.4.0.19", {"start": v(-59.08, 11.2) * mm, "end": v(-56.62, 11.2) * mm});
            skLineSegment(sketch, "E4.4.0.21", {"start": v(-72.08, 11.2) * mm, "end": v(-69.62, 11.2) * mm});
            skLineSegment(sketch, "E4.4.0.22", {"start": v(-65.58, 10.21) * mm, "end": v(-63.12, 10.21) * mm});
            skLineSegment(sketch, "E4.4.0.23", {"start": v(-85.08, 11.2) * mm, "end": v(-82.62, 11.2) * mm});
            skLineSegment(sketch, "E4.4.0.24", {"start": v(-78.58, 10.21) * mm, "end": v(-76.12, 10.21) * mm});
            skLineSegment(sketch, "E4.4.0.25", {"start": v(-98.08, 10.21) * mm, "end": v(-95.62, 10.21) * mm});
            skLineSegment(sketch, "E4.4.0.26", {"start": v(-98.08, 11.2) * mm, "end": v(-95.62, 11.2) * mm});
            skLineSegment(sketch, "E4.4.0.27", {"start": v(-101.33, 11.2) * mm, "end": v(-98.87, 11.2) * mm});
            skLineSegment(sketch, "E4.4.0.28", {"start": v(-65.58, 11.2) * mm, "end": v(-63.12, 11.2) * mm});
            skLineSegment(sketch, "E4.4.0.29", {"start": v(-78.58, 11.2) * mm, "end": v(-76.12, 11.2) * mm});
            skLineSegment(sketch, "E4.4.0.30", {"start": v(-91.58, 11.2) * mm, "end": v(-89.12, 11.2) * mm});
            skLineSegment(sketch, "E4.4.0.32", {"start": v(-94.83, 10.21) * mm, "end": v(-92.37, 10.21) * mm});
            skLineSegment(sketch, "E4.4.0.33", {"start": v(-101.33, 10.21) * mm, "end": v(-98.08, 10.21) * mm, "construction": true});
            skLineSegment(sketch, "E4.4.0.35", {"start": v(-68.83, 10.21) * mm, "end": v(-66.37, 10.21) * mm});
            skLineSegment(sketch, "E4.4.0.36", {"start": v(-81.83, 10.21) * mm, "end": v(-79.37, 10.21) * mm});
            skLineSegment(sketch, "E4.4.0.37", {"start": v(-101.33, 10.21) * mm, "end": v(-98.87, 10.21) * mm});
            skLineSegment(sketch, "E4.4.0.38", {"start": v(-94.83, 11.2) * mm, "end": v(-94.83, 10.21) * mm});
            skLineSegment(sketch, "E4.4.0.41", {"start": v(-59.87, 11.2) * mm, "end": v(-59.87, 10.21) * mm});
            skLineSegment(sketch, "E4.4.0.42", {"start": v(-72.87, 11.2) * mm, "end": v(-72.87, 10.21) * mm});
            skLineSegment(sketch, "E4.4.0.43", {"start": v(-68.83, 11.2) * mm, "end": v(-68.83, 10.21) * mm});
            skLineSegment(sketch, "E4.4.0.44", {"start": v(-85.87, 11.2) * mm, "end": v(-85.87, 10.21) * mm});
            skLineSegment(sketch, "E4.4.0.45", {"start": v(-81.83, 11.2) * mm, "end": v(-81.83, 10.21) * mm});
            skLineSegment(sketch, "E4.4.0.46", {"start": v(-62.33, 11.2) * mm, "end": v(-62.33, 10.21) * mm});
            skLineSegment(sketch, "E4.4.0.47", {"start": v(-75.33, 11.2) * mm, "end": v(-75.33, 10.21) * mm});
            skLineSegment(sketch, "E4.4.0.48", {"start": v(-88.33, 11.2) * mm, "end": v(-88.33, 10.21) * mm});
            skLineSegment(sketch, "E4.4.0.50", {"start": v(-92.37, 11.2) * mm, "end": v(-92.37, 10.21) * mm});
            skLineSegment(sketch, "E4.4.0.52", {"start": v(-66.37, 11.2) * mm, "end": v(-66.37, 10.21) * mm});
            skLineSegment(sketch, "E4.4.0.53", {"start": v(-79.37, 11.2) * mm, "end": v(-79.37, 10.21) * mm});
            skLineSegment(sketch, "E4.4.0.54", {"start": v(-98.87, 11.2) * mm, "end": v(-98.87, 10.21) * mm});
            skLineSegment(sketch, "E4.4.0.55", {"start": v(-101.33, 11.2) * mm, "end": v(-101.33, 10.21) * mm});
            skLineSegment(sketch, "E4.4.0.56", {"start": v(-98.08, 11.2) * mm, "end": v(-98.08, 10.21) * mm});
            skLineSegment(sketch, "E4.4.0.58", {"start": v(-59.08, 11.2) * mm, "end": v(-59.08, 10.21) * mm});
            skLineSegment(sketch, "E4.4.0.59", {"start": v(-72.08, 11.2) * mm, "end": v(-72.08, 10.21) * mm});
            skLineSegment(sketch, "E4.4.0.60", {"start": v(-85.08, 11.2) * mm, "end": v(-85.08, 10.21) * mm});
            skLineSegment(sketch, "E4.4.0.61", {"start": v(-65.58, 11.2) * mm, "end": v(-65.58, 10.21) * mm});
            skLineSegment(sketch, "E4.4.0.62", {"start": v(-78.58, 11.2) * mm, "end": v(-78.58, 10.21) * mm});
            skLineSegment(sketch, "E4.4.0.63", {"start": v(-91.58, 11.2) * mm, "end": v(-91.58, 10.21) * mm});
            skLineSegment(sketch, "E4.4.0.65", {"start": v(-95.62, 11.2) * mm, "end": v(-95.62, 10.21) * mm});
            skLineSegment(sketch, "E4.4.0.67", {"start": v(-56.62, 11.2) * mm, "end": v(-56.62, 10.21) * mm});
            skLineSegment(sketch, "E4.4.0.68", {"start": v(-69.62, 11.2) * mm, "end": v(-69.62, 10.21) * mm});
            skLineSegment(sketch, "E4.4.0.69", {"start": v(-82.62, 11.2) * mm, "end": v(-82.62, 10.21) * mm});
            skLineSegment(sketch, "E4.4.0.70", {"start": v(-63.12, 11.2) * mm, "end": v(-63.12, 10.21) * mm});
            skLineSegment(sketch, "E4.4.0.71", {"start": v(-76.12, 11.2) * mm, "end": v(-76.12, 10.21) * mm});
            skLineSegment(sketch, "E4.4.0.72", {"start": v(-89.12, 11.2) * mm, "end": v(-89.12, 10.21) * mm});
            skLineSegment(sketch, "E4.5.0.1", {"start": v(-88.32, 8.81) * mm, "end": v(-85.86, 8.81) * mm});
            skLineSegment(sketch, "E4.5.0.2", {"start": v(-81.82, 9.8) * mm, "end": v(-79.36, 9.8) * mm});
            skLineSegment(sketch, "E4.5.0.3", {"start": v(-62.32, 9.8) * mm, "end": v(-59.86, 9.8) * mm});
            skLineSegment(sketch, "E4.5.0.4", {"start": v(-62.32, 8.81) * mm, "end": v(-59.86, 8.81) * mm});
            skLineSegment(sketch, "E4.5.0.5", {"start": v(-68.82, 9.8) * mm, "end": v(-66.36, 9.8) * mm});
            skLineSegment(sketch, "E4.5.0.7", {"start": v(-88.32, 9.8) * mm, "end": v(-85.86, 9.8) * mm});
            skLineSegment(sketch, "E4.5.0.8", {"start": v(-75.32, 9.8) * mm, "end": v(-72.86, 9.8) * mm});
            skLineSegment(sketch, "E4.5.0.10", {"start": v(-94.82, 9.8) * mm, "end": v(-92.36, 9.8) * mm});
            skLineSegment(sketch, "E4.5.0.12", {"start": v(-75.32, 8.81) * mm, "end": v(-72.86, 8.81) * mm});
            skLineSegment(sketch, "E4.5.0.14", {"start": v(-59.07, 8.81) * mm, "end": v(-56.61, 8.81) * mm});
            skLineSegment(sketch, "E4.5.0.15", {"start": v(-72.07, 8.81) * mm, "end": v(-69.61, 8.81) * mm});
            skLineSegment(sketch, "E4.5.0.16", {"start": v(-85.07, 8.81) * mm, "end": v(-82.61, 8.81) * mm});
            skLineSegment(sketch, "E4.5.0.17", {"start": v(-91.57, 8.81) * mm, "end": v(-89.11, 8.81) * mm});
            skLineSegment(sketch, "E4.5.0.19", {"start": v(-59.07, 9.8) * mm, "end": v(-56.61, 9.8) * mm});
            skLineSegment(sketch, "E4.5.0.21", {"start": v(-72.07, 9.8) * mm, "end": v(-69.61, 9.8) * mm});
            skLineSegment(sketch, "E4.5.0.22", {"start": v(-65.57, 8.81) * mm, "end": v(-63.11, 8.81) * mm});
            skLineSegment(sketch, "E4.5.0.23", {"start": v(-85.07, 9.8) * mm, "end": v(-82.61, 9.8) * mm});
            skLineSegment(sketch, "E4.5.0.24", {"start": v(-78.57, 8.81) * mm, "end": v(-76.11, 8.81) * mm});
            skLineSegment(sketch, "E4.5.0.25", {"start": v(-98.07, 8.81) * mm, "end": v(-95.61, 8.81) * mm});
            skLineSegment(sketch, "E4.5.0.26", {"start": v(-98.07, 9.8) * mm, "end": v(-95.61, 9.8) * mm});
            skLineSegment(sketch, "E4.5.0.27", {"start": v(-101.32, 9.8) * mm, "end": v(-98.86, 9.8) * mm});
            skLineSegment(sketch, "E4.5.0.28", {"start": v(-65.57, 9.8) * mm, "end": v(-63.11, 9.8) * mm});
            skLineSegment(sketch, "E4.5.0.29", {"start": v(-78.57, 9.8) * mm, "end": v(-76.11, 9.8) * mm});
            skLineSegment(sketch, "E4.5.0.30", {"start": v(-91.57, 9.8) * mm, "end": v(-89.11, 9.8) * mm});
            skLineSegment(sketch, "E4.5.0.32", {"start": v(-94.82, 8.81) * mm, "end": v(-92.36, 8.81) * mm});
            skLineSegment(sketch, "E4.5.0.33", {"start": v(-101.32, 8.81) * mm, "end": v(-98.07, 8.81) * mm, "construction": true});
            skLineSegment(sketch, "E4.5.0.35", {"start": v(-68.82, 8.81) * mm, "end": v(-66.36, 8.81) * mm});
            skLineSegment(sketch, "E4.5.0.36", {"start": v(-81.82, 8.81) * mm, "end": v(-79.36, 8.81) * mm});
            skLineSegment(sketch, "E4.5.0.37", {"start": v(-101.32, 8.81) * mm, "end": v(-98.86, 8.81) * mm});
            skLineSegment(sketch, "E4.5.0.38", {"start": v(-94.82, 9.8) * mm, "end": v(-94.82, 8.81) * mm});
            skLineSegment(sketch, "E4.5.0.41", {"start": v(-59.86, 9.8) * mm, "end": v(-59.86, 8.81) * mm});
            skLineSegment(sketch, "E4.5.0.42", {"start": v(-72.86, 9.8) * mm, "end": v(-72.86, 8.81) * mm});
            skLineSegment(sketch, "E4.5.0.43", {"start": v(-68.82, 9.8) * mm, "end": v(-68.82, 8.81) * mm});
            skLineSegment(sketch, "E4.5.0.44", {"start": v(-85.86, 9.8) * mm, "end": v(-85.86, 8.81) * mm});
            skLineSegment(sketch, "E4.5.0.45", {"start": v(-81.82, 9.8) * mm, "end": v(-81.82, 8.81) * mm});
            skLineSegment(sketch, "E4.5.0.46", {"start": v(-62.32, 9.8) * mm, "end": v(-62.32, 8.81) * mm});
            skLineSegment(sketch, "E4.5.0.47", {"start": v(-75.32, 9.8) * mm, "end": v(-75.32, 8.81) * mm});
            skLineSegment(sketch, "E4.5.0.48", {"start": v(-88.32, 9.8) * mm, "end": v(-88.32, 8.81) * mm});
            skLineSegment(sketch, "E4.5.0.50", {"start": v(-92.36, 9.8) * mm, "end": v(-92.36, 8.81) * mm});
            skLineSegment(sketch, "E4.5.0.52", {"start": v(-66.36, 9.8) * mm, "end": v(-66.36, 8.81) * mm});
            skLineSegment(sketch, "E4.5.0.53", {"start": v(-79.36, 9.8) * mm, "end": v(-79.36, 8.81) * mm});
            skLineSegment(sketch, "E4.5.0.54", {"start": v(-98.86, 9.8) * mm, "end": v(-98.86, 8.81) * mm});
            skLineSegment(sketch, "E4.5.0.55", {"start": v(-101.32, 9.8) * mm, "end": v(-101.32, 8.81) * mm});
            skLineSegment(sketch, "E4.5.0.56", {"start": v(-98.07, 9.8) * mm, "end": v(-98.07, 8.81) * mm});
            skLineSegment(sketch, "E4.5.0.58", {"start": v(-59.07, 9.8) * mm, "end": v(-59.07, 8.81) * mm});
            skLineSegment(sketch, "E4.5.0.59", {"start": v(-72.07, 9.8) * mm, "end": v(-72.07, 8.81) * mm});
            skLineSegment(sketch, "E4.5.0.60", {"start": v(-85.07, 9.8) * mm, "end": v(-85.07, 8.81) * mm});
            skLineSegment(sketch, "E4.5.0.61", {"start": v(-65.57, 9.8) * mm, "end": v(-65.57, 8.81) * mm});
            skLineSegment(sketch, "E4.5.0.62", {"start": v(-78.57, 9.8) * mm, "end": v(-78.57, 8.81) * mm});
            skLineSegment(sketch, "E4.5.0.63", {"start": v(-91.57, 9.8) * mm, "end": v(-91.57, 8.81) * mm});
            skLineSegment(sketch, "E4.5.0.65", {"start": v(-95.61, 9.8) * mm, "end": v(-95.61, 8.81) * mm});
            skLineSegment(sketch, "E4.5.0.67", {"start": v(-56.61, 9.8) * mm, "end": v(-56.61, 8.81) * mm});
            skLineSegment(sketch, "E4.5.0.68", {"start": v(-69.61, 9.8) * mm, "end": v(-69.61, 8.81) * mm});
            skLineSegment(sketch, "E4.5.0.69", {"start": v(-82.61, 9.8) * mm, "end": v(-82.61, 8.81) * mm});
            skLineSegment(sketch, "E4.5.0.70", {"start": v(-63.11, 9.8) * mm, "end": v(-63.11, 8.81) * mm});
            skLineSegment(sketch, "E4.5.0.71", {"start": v(-76.11, 9.8) * mm, "end": v(-76.11, 8.81) * mm});
            skLineSegment(sketch, "E4.5.0.72", {"start": v(-89.11, 9.8) * mm, "end": v(-89.11, 8.81) * mm});
            skLineSegment(sketch, "E4.6.0.1", {"start": v(-88.32, 7.41) * mm, "end": v(-85.86, 7.41) * mm});
            skLineSegment(sketch, "E4.6.0.2", {"start": v(-81.82, 8.39) * mm, "end": v(-79.36, 8.39) * mm});
            skLineSegment(sketch, "E4.6.0.3", {"start": v(-62.32, 8.39) * mm, "end": v(-59.86, 8.39) * mm});
            skLineSegment(sketch, "E4.6.0.4", {"start": v(-62.32, 7.41) * mm, "end": v(-59.86, 7.41) * mm});
            skLineSegment(sketch, "E4.6.0.5", {"start": v(-68.82, 8.39) * mm, "end": v(-66.36, 8.39) * mm});
            skLineSegment(sketch, "E4.6.0.7", {"start": v(-88.32, 8.39) * mm, "end": v(-85.86, 8.39) * mm});
            skLineSegment(sketch, "E4.6.0.8", {"start": v(-75.32, 8.39) * mm, "end": v(-72.86, 8.39) * mm});
            skLineSegment(sketch, "E4.6.0.10", {"start": v(-94.82, 8.39) * mm, "end": v(-92.36, 8.39) * mm});
            skLineSegment(sketch, "E4.6.0.12", {"start": v(-75.32, 7.41) * mm, "end": v(-72.86, 7.41) * mm});
            skLineSegment(sketch, "E4.6.0.14", {"start": v(-59.07, 7.41) * mm, "end": v(-56.6, 7.41) * mm});
            skLineSegment(sketch, "E4.6.0.15", {"start": v(-72.07, 7.41) * mm, "end": v(-69.6, 7.41) * mm});
            skLineSegment(sketch, "E4.6.0.16", {"start": v(-85.07, 7.41) * mm, "end": v(-82.6, 7.41) * mm});
            skLineSegment(sketch, "E4.6.0.17", {"start": v(-91.57, 7.41) * mm, "end": v(-89.1, 7.41) * mm});
            skLineSegment(sketch, "E4.6.0.19", {"start": v(-59.07, 8.39) * mm, "end": v(-56.6, 8.39) * mm});
            skLineSegment(sketch, "E4.6.0.21", {"start": v(-72.07, 8.39) * mm, "end": v(-69.6, 8.39) * mm});
            skLineSegment(sketch, "E4.6.0.22", {"start": v(-65.57, 7.41) * mm, "end": v(-63.1, 7.41) * mm});
            skLineSegment(sketch, "E4.6.0.23", {"start": v(-85.07, 8.39) * mm, "end": v(-82.6, 8.39) * mm});
            skLineSegment(sketch, "E4.6.0.24", {"start": v(-78.57, 7.41) * mm, "end": v(-76.1, 7.41) * mm});
            skLineSegment(sketch, "E4.6.0.25", {"start": v(-98.07, 7.41) * mm, "end": v(-95.6, 7.41) * mm});
            skLineSegment(sketch, "E4.6.0.26", {"start": v(-98.07, 8.39) * mm, "end": v(-95.6, 8.39) * mm});
            skLineSegment(sketch, "E4.6.0.27", {"start": v(-101.32, 8.39) * mm, "end": v(-98.86, 8.39) * mm});
            skLineSegment(sketch, "E4.6.0.28", {"start": v(-65.57, 8.39) * mm, "end": v(-63.1, 8.39) * mm});
            skLineSegment(sketch, "E4.6.0.29", {"start": v(-78.57, 8.39) * mm, "end": v(-76.1, 8.39) * mm});
            skLineSegment(sketch, "E4.6.0.30", {"start": v(-91.57, 8.39) * mm, "end": v(-89.1, 8.39) * mm});
            skLineSegment(sketch, "E4.6.0.32", {"start": v(-94.82, 7.41) * mm, "end": v(-92.36, 7.41) * mm});
            skLineSegment(sketch, "E4.6.0.33", {"start": v(-101.32, 7.41) * mm, "end": v(-98.07, 7.41) * mm, "construction": true});
            skLineSegment(sketch, "E4.6.0.35", {"start": v(-68.82, 7.41) * mm, "end": v(-66.36, 7.41) * mm});
            skLineSegment(sketch, "E4.6.0.36", {"start": v(-81.82, 7.41) * mm, "end": v(-79.36, 7.41) * mm});
            skLineSegment(sketch, "E4.6.0.37", {"start": v(-101.32, 7.41) * mm, "end": v(-98.86, 7.41) * mm});
            skLineSegment(sketch, "E4.6.0.38", {"start": v(-94.82, 8.39) * mm, "end": v(-94.82, 7.41) * mm});
            skLineSegment(sketch, "E4.6.0.41", {"start": v(-59.86, 8.39) * mm, "end": v(-59.86, 7.41) * mm});
            skLineSegment(sketch, "E4.6.0.42", {"start": v(-72.86, 8.39) * mm, "end": v(-72.86, 7.41) * mm});
            skLineSegment(sketch, "E4.6.0.43", {"start": v(-68.82, 8.39) * mm, "end": v(-68.82, 7.41) * mm});
            skLineSegment(sketch, "E4.6.0.44", {"start": v(-85.86, 8.39) * mm, "end": v(-85.86, 7.41) * mm});
            skLineSegment(sketch, "E4.6.0.45", {"start": v(-81.82, 8.39) * mm, "end": v(-81.82, 7.41) * mm});
            skLineSegment(sketch, "E4.6.0.46", {"start": v(-62.32, 8.39) * mm, "end": v(-62.32, 7.41) * mm});
            skLineSegment(sketch, "E4.6.0.47", {"start": v(-75.32, 8.39) * mm, "end": v(-75.32, 7.41) * mm});
            skLineSegment(sketch, "E4.6.0.48", {"start": v(-88.32, 8.39) * mm, "end": v(-88.32, 7.41) * mm});
            skLineSegment(sketch, "E4.6.0.50", {"start": v(-92.36, 8.39) * mm, "end": v(-92.36, 7.41) * mm});
            skLineSegment(sketch, "E4.6.0.52", {"start": v(-66.36, 8.39) * mm, "end": v(-66.36, 7.41) * mm});
            skLineSegment(sketch, "E4.6.0.53", {"start": v(-79.36, 8.39) * mm, "end": v(-79.36, 7.41) * mm});
            skLineSegment(sketch, "E4.6.0.54", {"start": v(-98.86, 8.39) * mm, "end": v(-98.86, 7.41) * mm});
            skLineSegment(sketch, "E4.6.0.55", {"start": v(-101.32, 8.39) * mm, "end": v(-101.32, 7.41) * mm});
            skLineSegment(sketch, "E4.6.0.56", {"start": v(-98.07, 8.39) * mm, "end": v(-98.07, 7.41) * mm});
            skLineSegment(sketch, "E4.6.0.58", {"start": v(-59.07, 8.39) * mm, "end": v(-59.07, 7.41) * mm});
            skLineSegment(sketch, "E4.6.0.59", {"start": v(-72.07, 8.39) * mm, "end": v(-72.07, 7.41) * mm});
            skLineSegment(sketch, "E4.6.0.60", {"start": v(-85.07, 8.39) * mm, "end": v(-85.07, 7.41) * mm});
            skLineSegment(sketch, "E4.6.0.61", {"start": v(-65.57, 8.39) * mm, "end": v(-65.57, 7.41) * mm});
            skLineSegment(sketch, "E4.6.0.62", {"start": v(-78.57, 8.39) * mm, "end": v(-78.57, 7.41) * mm});
            skLineSegment(sketch, "E4.6.0.63", {"start": v(-91.57, 8.39) * mm, "end": v(-91.57, 7.41) * mm});
            skLineSegment(sketch, "E4.6.0.65", {"start": v(-95.6, 8.39) * mm, "end": v(-95.6, 7.41) * mm});
            skLineSegment(sketch, "E4.6.0.67", {"start": v(-56.6, 8.39) * mm, "end": v(-56.6, 7.41) * mm});
            skLineSegment(sketch, "E4.6.0.68", {"start": v(-69.6, 8.39) * mm, "end": v(-69.6, 7.41) * mm});
            skLineSegment(sketch, "E4.6.0.69", {"start": v(-82.6, 8.39) * mm, "end": v(-82.6, 7.41) * mm});
            skLineSegment(sketch, "E4.6.0.70", {"start": v(-63.1, 8.39) * mm, "end": v(-63.1, 7.41) * mm});
            skLineSegment(sketch, "E4.6.0.71", {"start": v(-76.1, 8.39) * mm, "end": v(-76.1, 7.41) * mm});
            skLineSegment(sketch, "E4.6.0.72", {"start": v(-89.1, 8.39) * mm, "end": v(-89.1, 7.41) * mm});
            skLineSegment(sketch, "E4.7.0.1", {"start": v(-88.31, 6) * mm, "end": v(-85.85, 6) * mm});
            skLineSegment(sketch, "E4.7.0.2", {"start": v(-81.81, 6.99) * mm, "end": v(-79.35, 6.99) * mm});
            skLineSegment(sketch, "E4.7.0.3", {"start": v(-62.31, 6.99) * mm, "end": v(-59.85, 6.99) * mm});
            skLineSegment(sketch, "E4.7.0.4", {"start": v(-62.31, 6) * mm, "end": v(-59.85, 6) * mm});
            skLineSegment(sketch, "E4.7.0.5", {"start": v(-68.81, 6.99) * mm, "end": v(-66.35, 6.99) * mm});
            skLineSegment(sketch, "E4.7.0.7", {"start": v(-88.31, 6.99) * mm, "end": v(-85.85, 6.99) * mm});
            skLineSegment(sketch, "E4.7.0.8", {"start": v(-75.31, 6.99) * mm, "end": v(-72.85, 6.99) * mm});
            skLineSegment(sketch, "E4.7.0.10", {"start": v(-94.81, 6.99) * mm, "end": v(-92.35, 6.99) * mm});
            skLineSegment(sketch, "E4.7.0.12", {"start": v(-75.31, 6) * mm, "end": v(-72.85, 6) * mm});
            skLineSegment(sketch, "E4.7.0.14", {"start": v(-59.06, 6) * mm, "end": v(-56.6, 6) * mm});
            skLineSegment(sketch, "E4.7.0.15", {"start": v(-72.06, 6) * mm, "end": v(-69.6, 6) * mm});
            skLineSegment(sketch, "E4.7.0.16", {"start": v(-85.06, 6) * mm, "end": v(-82.6, 6) * mm});
            skLineSegment(sketch, "E4.7.0.17", {"start": v(-91.56, 6) * mm, "end": v(-89.1, 6) * mm});
            skLineSegment(sketch, "E4.7.0.19", {"start": v(-59.06, 6.99) * mm, "end": v(-56.6, 6.99) * mm});
            skLineSegment(sketch, "E4.7.0.21", {"start": v(-72.06, 6.99) * mm, "end": v(-69.6, 6.99) * mm});
            skLineSegment(sketch, "E4.7.0.22", {"start": v(-65.56, 6) * mm, "end": v(-63.1, 6) * mm});
            skLineSegment(sketch, "E4.7.0.23", {"start": v(-85.06, 6.99) * mm, "end": v(-82.6, 6.99) * mm});
            skLineSegment(sketch, "E4.7.0.24", {"start": v(-78.56, 6) * mm, "end": v(-76.1, 6) * mm});
            skLineSegment(sketch, "E4.7.0.25", {"start": v(-98.06, 6) * mm, "end": v(-95.6, 6) * mm});
            skLineSegment(sketch, "E4.7.0.26", {"start": v(-98.06, 6.99) * mm, "end": v(-95.6, 6.99) * mm});
            skLineSegment(sketch, "E4.7.0.27", {"start": v(-101.31, 6.99) * mm, "end": v(-98.85, 6.99) * mm});
            skLineSegment(sketch, "E4.7.0.28", {"start": v(-65.56, 6.99) * mm, "end": v(-63.1, 6.99) * mm});
            skLineSegment(sketch, "E4.7.0.29", {"start": v(-78.56, 6.99) * mm, "end": v(-76.1, 6.99) * mm});
            skLineSegment(sketch, "E4.7.0.30", {"start": v(-91.56, 6.99) * mm, "end": v(-89.1, 6.99) * mm});
            skLineSegment(sketch, "E4.7.0.32", {"start": v(-94.81, 6) * mm, "end": v(-92.35, 6) * mm});
            skLineSegment(sketch, "E4.7.0.33", {"start": v(-101.31, 6) * mm, "end": v(-98.06, 6) * mm, "construction": true});
            skLineSegment(sketch, "E4.7.0.35", {"start": v(-68.81, 6) * mm, "end": v(-66.35, 6) * mm});
            skLineSegment(sketch, "E4.7.0.36", {"start": v(-81.81, 6) * mm, "end": v(-79.35, 6) * mm});
            skLineSegment(sketch, "E4.7.0.37", {"start": v(-101.31, 6) * mm, "end": v(-98.85, 6) * mm});
            skLineSegment(sketch, "E4.7.0.38", {"start": v(-94.81, 6.99) * mm, "end": v(-94.81, 6) * mm});
            skLineSegment(sketch, "E4.7.0.41", {"start": v(-59.85, 6.99) * mm, "end": v(-59.85, 6) * mm});
            skLineSegment(sketch, "E4.7.0.42", {"start": v(-72.85, 6.99) * mm, "end": v(-72.85, 6) * mm});
            skLineSegment(sketch, "E4.7.0.43", {"start": v(-68.81, 6.99) * mm, "end": v(-68.81, 6) * mm});
            skLineSegment(sketch, "E4.7.0.44", {"start": v(-85.85, 6.99) * mm, "end": v(-85.85, 6) * mm});
            skLineSegment(sketch, "E4.7.0.45", {"start": v(-81.81, 6.99) * mm, "end": v(-81.81, 6) * mm});
            skLineSegment(sketch, "E4.7.0.46", {"start": v(-62.31, 6.99) * mm, "end": v(-62.31, 6) * mm});
            skLineSegment(sketch, "E4.7.0.47", {"start": v(-75.31, 6.99) * mm, "end": v(-75.31, 6) * mm});
            skLineSegment(sketch, "E4.7.0.48", {"start": v(-88.31, 6.99) * mm, "end": v(-88.31, 6) * mm});
            skLineSegment(sketch, "E4.7.0.50", {"start": v(-92.35, 6.99) * mm, "end": v(-92.35, 6) * mm});
            skLineSegment(sketch, "E4.7.0.52", {"start": v(-66.35, 6.99) * mm, "end": v(-66.35, 6) * mm});
            skLineSegment(sketch, "E4.7.0.53", {"start": v(-79.35, 6.99) * mm, "end": v(-79.35, 6) * mm});
            skLineSegment(sketch, "E4.7.0.54", {"start": v(-98.85, 6.99) * mm, "end": v(-98.85, 6) * mm});
            skLineSegment(sketch, "E4.7.0.55", {"start": v(-101.31, 6.99) * mm, "end": v(-101.31, 6) * mm});
            skLineSegment(sketch, "E4.7.0.56", {"start": v(-98.06, 6.99) * mm, "end": v(-98.06, 6) * mm});
            skLineSegment(sketch, "E4.7.0.58", {"start": v(-59.06, 6.99) * mm, "end": v(-59.06, 6) * mm});
            skLineSegment(sketch, "E4.7.0.59", {"start": v(-72.06, 6.99) * mm, "end": v(-72.06, 6) * mm});
            skLineSegment(sketch, "E4.7.0.60", {"start": v(-85.06, 6.99) * mm, "end": v(-85.06, 6) * mm});
            skLineSegment(sketch, "E4.7.0.61", {"start": v(-65.56, 6.99) * mm, "end": v(-65.56, 6) * mm});
            skLineSegment(sketch, "E4.7.0.62", {"start": v(-78.56, 6.99) * mm, "end": v(-78.56, 6) * mm});
            skLineSegment(sketch, "E4.7.0.63", {"start": v(-91.56, 6.99) * mm, "end": v(-91.56, 6) * mm});
            skLineSegment(sketch, "E4.7.0.65", {"start": v(-95.6, 6.99) * mm, "end": v(-95.6, 6) * mm});
            skLineSegment(sketch, "E4.7.0.67", {"start": v(-56.6, 6.99) * mm, "end": v(-56.6, 6) * mm});
            skLineSegment(sketch, "E4.7.0.68", {"start": v(-69.6, 6.99) * mm, "end": v(-69.6, 6) * mm});
            skLineSegment(sketch, "E4.7.0.69", {"start": v(-82.6, 6.99) * mm, "end": v(-82.6, 6) * mm});
            skLineSegment(sketch, "E4.7.0.70", {"start": v(-63.1, 6.99) * mm, "end": v(-63.1, 6) * mm});
            skLineSegment(sketch, "E4.7.0.71", {"start": v(-76.1, 6.99) * mm, "end": v(-76.1, 6) * mm});
            skLineSegment(sketch, "E4.7.0.72", {"start": v(-89.1, 6.99) * mm, "end": v(-89.1, 6) * mm});
            skLineSegment(sketch, "E4.8.0.1", {"start": v(-88.3, 4.6) * mm, "end": v(-85.84, 4.6) * mm});
            skLineSegment(sketch, "E4.8.0.2", {"start": v(-81.8, 5.59) * mm, "end": v(-79.34, 5.59) * mm});
            skLineSegment(sketch, "E4.8.0.3", {"start": v(-62.3, 5.59) * mm, "end": v(-59.84, 5.59) * mm});
            skLineSegment(sketch, "E4.8.0.4", {"start": v(-62.3, 4.6) * mm, "end": v(-59.84, 4.6) * mm});
            skLineSegment(sketch, "E4.8.0.5", {"start": v(-68.8, 5.59) * mm, "end": v(-66.34, 5.59) * mm});
            skLineSegment(sketch, "E4.8.0.7", {"start": v(-88.3, 5.59) * mm, "end": v(-85.84, 5.59) * mm});
            skLineSegment(sketch, "E4.8.0.8", {"start": v(-75.3, 5.59) * mm, "end": v(-72.84, 5.59) * mm});
            skLineSegment(sketch, "E4.8.0.10", {"start": v(-94.8, 5.59) * mm, "end": v(-92.34, 5.59) * mm});
            skLineSegment(sketch, "E4.8.0.12", {"start": v(-75.3, 4.6) * mm, "end": v(-72.84, 4.6) * mm});
            skLineSegment(sketch, "E4.8.0.14", {"start": v(-59.06, 4.6) * mm, "end": v(-56.6, 4.6) * mm});
            skLineSegment(sketch, "E4.8.0.15", {"start": v(-72.06, 4.6) * mm, "end": v(-69.6, 4.6) * mm});
            skLineSegment(sketch, "E4.8.0.16", {"start": v(-85.06, 4.6) * mm, "end": v(-82.6, 4.6) * mm});
            skLineSegment(sketch, "E4.8.0.17", {"start": v(-91.56, 4.6) * mm, "end": v(-89.1, 4.6) * mm});
            skLineSegment(sketch, "E4.8.0.19", {"start": v(-59.06, 5.59) * mm, "end": v(-56.6, 5.59) * mm});
            skLineSegment(sketch, "E4.8.0.21", {"start": v(-72.06, 5.59) * mm, "end": v(-69.6, 5.59) * mm});
            skLineSegment(sketch, "E4.8.0.22", {"start": v(-65.56, 4.6) * mm, "end": v(-63.1, 4.6) * mm});
            skLineSegment(sketch, "E4.8.0.23", {"start": v(-85.06, 5.59) * mm, "end": v(-82.6, 5.59) * mm});
            skLineSegment(sketch, "E4.8.0.24", {"start": v(-78.56, 4.6) * mm, "end": v(-76.1, 4.6) * mm});
            skLineSegment(sketch, "E4.8.0.25", {"start": v(-98.06, 4.6) * mm, "end": v(-95.6, 4.6) * mm});
            skLineSegment(sketch, "E4.8.0.26", {"start": v(-98.06, 5.59) * mm, "end": v(-95.6, 5.59) * mm});
            skLineSegment(sketch, "E4.8.0.27", {"start": v(-101.3, 5.59) * mm, "end": v(-98.84, 5.59) * mm});
            skLineSegment(sketch, "E4.8.0.28", {"start": v(-65.56, 5.59) * mm, "end": v(-63.1, 5.59) * mm});
            skLineSegment(sketch, "E4.8.0.29", {"start": v(-78.56, 5.59) * mm, "end": v(-76.1, 5.59) * mm});
            skLineSegment(sketch, "E4.8.0.30", {"start": v(-91.56, 5.59) * mm, "end": v(-89.1, 5.59) * mm});
            skLineSegment(sketch, "E4.8.0.32", {"start": v(-94.8, 4.6) * mm, "end": v(-92.34, 4.6) * mm});
            skLineSegment(sketch, "E4.8.0.33", {"start": v(-101.3, 4.6) * mm, "end": v(-98.06, 4.6) * mm, "construction": true});
            skLineSegment(sketch, "E4.8.0.35", {"start": v(-68.8, 4.6) * mm, "end": v(-66.34, 4.6) * mm});
            skLineSegment(sketch, "E4.8.0.36", {"start": v(-81.8, 4.6) * mm, "end": v(-79.34, 4.6) * mm});
            skLineSegment(sketch, "E4.8.0.37", {"start": v(-101.3, 4.6) * mm, "end": v(-98.84, 4.6) * mm});
            skLineSegment(sketch, "E4.8.0.38", {"start": v(-94.8, 5.59) * mm, "end": v(-94.8, 4.6) * mm});
            skLineSegment(sketch, "E4.8.0.41", {"start": v(-59.84, 5.59) * mm, "end": v(-59.84, 4.6) * mm});
            skLineSegment(sketch, "E4.8.0.42", {"start": v(-72.84, 5.59) * mm, "end": v(-72.84, 4.6) * mm});
            skLineSegment(sketch, "E4.8.0.43", {"start": v(-68.8, 5.59) * mm, "end": v(-68.8, 4.6) * mm});
            skLineSegment(sketch, "E4.8.0.44", {"start": v(-85.84, 5.59) * mm, "end": v(-85.84, 4.6) * mm});
            skLineSegment(sketch, "E4.8.0.45", {"start": v(-81.8, 5.59) * mm, "end": v(-81.8, 4.6) * mm});
            skLineSegment(sketch, "E4.8.0.46", {"start": v(-62.3, 5.59) * mm, "end": v(-62.3, 4.6) * mm});
            skLineSegment(sketch, "E4.8.0.47", {"start": v(-75.3, 5.59) * mm, "end": v(-75.3, 4.6) * mm});
            skLineSegment(sketch, "E4.8.0.48", {"start": v(-88.3, 5.59) * mm, "end": v(-88.3, 4.6) * mm});
            skLineSegment(sketch, "E4.8.0.50", {"start": v(-92.34, 5.59) * mm, "end": v(-92.34, 4.6) * mm});
            skLineSegment(sketch, "E4.8.0.52", {"start": v(-66.34, 5.59) * mm, "end": v(-66.34, 4.6) * mm});
            skLineSegment(sketch, "E4.8.0.53", {"start": v(-79.34, 5.59) * mm, "end": v(-79.34, 4.6) * mm});
            skLineSegment(sketch, "E4.8.0.54", {"start": v(-98.84, 5.59) * mm, "end": v(-98.84, 4.6) * mm});
            skLineSegment(sketch, "E4.8.0.55", {"start": v(-101.3, 5.59) * mm, "end": v(-101.3, 4.6) * mm});
            skLineSegment(sketch, "E4.8.0.56", {"start": v(-98.06, 5.59) * mm, "end": v(-98.06, 4.6) * mm});
            skLineSegment(sketch, "E4.8.0.58", {"start": v(-59.06, 5.59) * mm, "end": v(-59.06, 4.6) * mm});
            skLineSegment(sketch, "E4.8.0.59", {"start": v(-72.06, 5.59) * mm, "end": v(-72.06, 4.6) * mm});
            skLineSegment(sketch, "E4.8.0.60", {"start": v(-85.06, 5.59) * mm, "end": v(-85.06, 4.6) * mm});
            skLineSegment(sketch, "E4.8.0.61", {"start": v(-65.56, 5.59) * mm, "end": v(-65.56, 4.6) * mm});
            skLineSegment(sketch, "E4.8.0.62", {"start": v(-78.56, 5.59) * mm, "end": v(-78.56, 4.6) * mm});
            skLineSegment(sketch, "E4.8.0.63", {"start": v(-91.56, 5.59) * mm, "end": v(-91.56, 4.6) * mm});
            skLineSegment(sketch, "E4.8.0.65", {"start": v(-95.6, 5.59) * mm, "end": v(-95.6, 4.6) * mm});
            skLineSegment(sketch, "E4.8.0.67", {"start": v(-56.6, 5.59) * mm, "end": v(-56.6, 4.6) * mm});
            skLineSegment(sketch, "E4.8.0.68", {"start": v(-69.6, 5.59) * mm, "end": v(-69.6, 4.6) * mm});
            skLineSegment(sketch, "E4.8.0.69", {"start": v(-82.6, 5.59) * mm, "end": v(-82.6, 4.6) * mm});
            skLineSegment(sketch, "E4.8.0.70", {"start": v(-63.1, 5.59) * mm, "end": v(-63.1, 4.6) * mm});
            skLineSegment(sketch, "E4.8.0.71", {"start": v(-76.1, 5.59) * mm, "end": v(-76.1, 4.6) * mm});
            skLineSegment(sketch, "E4.8.0.72", {"start": v(-89.1, 5.59) * mm, "end": v(-89.1, 4.6) * mm});
            skLineSegment(sketch, "E4.9.0.1", {"start": v(-88.3, 3.2) * mm, "end": v(-85.84, 3.2) * mm});
            skLineSegment(sketch, "E4.9.0.2", {"start": v(-81.8, 4.18) * mm, "end": v(-79.34, 4.18) * mm});
            skLineSegment(sketch, "E4.9.0.3", {"start": v(-62.3, 4.18) * mm, "end": v(-59.84, 4.18) * mm});
            skLineSegment(sketch, "E4.9.0.4", {"start": v(-62.3, 3.2) * mm, "end": v(-59.84, 3.2) * mm});
            skLineSegment(sketch, "E4.9.0.5", {"start": v(-68.8, 4.18) * mm, "end": v(-66.34, 4.18) * mm});
            skLineSegment(sketch, "E4.9.0.7", {"start": v(-88.3, 4.18) * mm, "end": v(-85.84, 4.18) * mm});
            skLineSegment(sketch, "E4.9.0.8", {"start": v(-75.3, 4.18) * mm, "end": v(-72.84, 4.18) * mm});
            skLineSegment(sketch, "E4.9.0.10", {"start": v(-94.8, 4.18) * mm, "end": v(-92.34, 4.18) * mm});
            skLineSegment(sketch, "E4.9.0.12", {"start": v(-75.3, 3.2) * mm, "end": v(-72.84, 3.2) * mm});
            skLineSegment(sketch, "E4.9.0.14", {"start": v(-59.05, 3.2) * mm, "end": v(-56.59, 3.2) * mm});
            skLineSegment(sketch, "E4.9.0.15", {"start": v(-72.05, 3.2) * mm, "end": v(-69.59, 3.2) * mm});
            skLineSegment(sketch, "E4.9.0.16", {"start": v(-85.05, 3.2) * mm, "end": v(-82.59, 3.2) * mm});
            skLineSegment(sketch, "E4.9.0.17", {"start": v(-91.55, 3.2) * mm, "end": v(-89.09, 3.2) * mm});
            skLineSegment(sketch, "E4.9.0.19", {"start": v(-59.05, 4.18) * mm, "end": v(-56.59, 4.18) * mm});
            skLineSegment(sketch, "E4.9.0.21", {"start": v(-72.05, 4.18) * mm, "end": v(-69.59, 4.18) * mm});
            skLineSegment(sketch, "E4.9.0.22", {"start": v(-65.55, 3.2) * mm, "end": v(-63.09, 3.2) * mm});
            skLineSegment(sketch, "E4.9.0.23", {"start": v(-85.05, 4.18) * mm, "end": v(-82.59, 4.18) * mm});
            skLineSegment(sketch, "E4.9.0.24", {"start": v(-78.55, 3.2) * mm, "end": v(-76.09, 3.2) * mm});
            skLineSegment(sketch, "E4.9.0.25", {"start": v(-98.05, 3.2) * mm, "end": v(-95.59, 3.2) * mm});
            skLineSegment(sketch, "E4.9.0.26", {"start": v(-98.05, 4.18) * mm, "end": v(-95.59, 4.18) * mm});
            skLineSegment(sketch, "E4.9.0.27", {"start": v(-101.3, 4.18) * mm, "end": v(-98.84, 4.18) * mm});
            skLineSegment(sketch, "E4.9.0.28", {"start": v(-65.55, 4.18) * mm, "end": v(-63.09, 4.18) * mm});
            skLineSegment(sketch, "E4.9.0.29", {"start": v(-78.55, 4.18) * mm, "end": v(-76.09, 4.18) * mm});
            skLineSegment(sketch, "E4.9.0.30", {"start": v(-91.55, 4.18) * mm, "end": v(-89.09, 4.18) * mm});
            skLineSegment(sketch, "E4.9.0.32", {"start": v(-94.8, 3.2) * mm, "end": v(-92.34, 3.2) * mm});
            skLineSegment(sketch, "E4.9.0.33", {"start": v(-101.3, 3.2) * mm, "end": v(-98.05, 3.2) * mm, "construction": true});
            skLineSegment(sketch, "E4.9.0.35", {"start": v(-68.8, 3.2) * mm, "end": v(-66.34, 3.2) * mm});
            skLineSegment(sketch, "E4.9.0.36", {"start": v(-81.8, 3.2) * mm, "end": v(-79.34, 3.2) * mm});
            skLineSegment(sketch, "E4.9.0.37", {"start": v(-101.3, 3.2) * mm, "end": v(-98.84, 3.2) * mm});
            skLineSegment(sketch, "E4.9.0.38", {"start": v(-94.8, 4.18) * mm, "end": v(-94.8, 3.2) * mm});
            skLineSegment(sketch, "E4.9.0.41", {"start": v(-59.84, 4.18) * mm, "end": v(-59.84, 3.2) * mm});
            skLineSegment(sketch, "E4.9.0.42", {"start": v(-72.84, 4.18) * mm, "end": v(-72.84, 3.2) * mm});
            skLineSegment(sketch, "E4.9.0.43", {"start": v(-68.8, 4.18) * mm, "end": v(-68.8, 3.2) * mm});
            skLineSegment(sketch, "E4.9.0.44", {"start": v(-85.84, 4.18) * mm, "end": v(-85.84, 3.2) * mm});
            skLineSegment(sketch, "E4.9.0.45", {"start": v(-81.8, 4.18) * mm, "end": v(-81.8, 3.2) * mm});
            skLineSegment(sketch, "E4.9.0.46", {"start": v(-62.3, 4.18) * mm, "end": v(-62.3, 3.2) * mm});
            skLineSegment(sketch, "E4.9.0.47", {"start": v(-75.3, 4.18) * mm, "end": v(-75.3, 3.2) * mm});
            skLineSegment(sketch, "E4.9.0.48", {"start": v(-88.3, 4.18) * mm, "end": v(-88.3, 3.2) * mm});
            skLineSegment(sketch, "E4.9.0.50", {"start": v(-92.34, 4.18) * mm, "end": v(-92.34, 3.2) * mm});
            skLineSegment(sketch, "E4.9.0.52", {"start": v(-66.34, 4.18) * mm, "end": v(-66.34, 3.2) * mm});
            skLineSegment(sketch, "E4.9.0.53", {"start": v(-79.34, 4.18) * mm, "end": v(-79.34, 3.2) * mm});
            skLineSegment(sketch, "E4.9.0.54", {"start": v(-98.84, 4.18) * mm, "end": v(-98.84, 3.2) * mm});
            skLineSegment(sketch, "E4.9.0.55", {"start": v(-101.3, 4.18) * mm, "end": v(-101.3, 3.2) * mm});
            skLineSegment(sketch, "E4.9.0.56", {"start": v(-98.05, 4.18) * mm, "end": v(-98.05, 3.2) * mm});
            skLineSegment(sketch, "E4.9.0.58", {"start": v(-59.05, 4.18) * mm, "end": v(-59.05, 3.2) * mm});
            skLineSegment(sketch, "E4.9.0.59", {"start": v(-72.05, 4.18) * mm, "end": v(-72.05, 3.2) * mm});
            skLineSegment(sketch, "E4.9.0.60", {"start": v(-85.05, 4.18) * mm, "end": v(-85.05, 3.2) * mm});
            skLineSegment(sketch, "E4.9.0.61", {"start": v(-65.55, 4.18) * mm, "end": v(-65.55, 3.2) * mm});
            skLineSegment(sketch, "E4.9.0.62", {"start": v(-78.55, 4.18) * mm, "end": v(-78.55, 3.2) * mm});
            skLineSegment(sketch, "E4.9.0.63", {"start": v(-91.55, 4.18) * mm, "end": v(-91.55, 3.2) * mm});
            skLineSegment(sketch, "E4.9.0.65", {"start": v(-95.59, 4.18) * mm, "end": v(-95.59, 3.2) * mm});
            skLineSegment(sketch, "E4.9.0.67", {"start": v(-56.59, 4.18) * mm, "end": v(-56.59, 3.2) * mm});
            skLineSegment(sketch, "E4.9.0.68", {"start": v(-69.59, 4.18) * mm, "end": v(-69.59, 3.2) * mm});
            skLineSegment(sketch, "E4.9.0.69", {"start": v(-82.59, 4.18) * mm, "end": v(-82.59, 3.2) * mm});
            skLineSegment(sketch, "E4.9.0.70", {"start": v(-63.09, 4.18) * mm, "end": v(-63.09, 3.2) * mm});
            skLineSegment(sketch, "E4.9.0.71", {"start": v(-76.09, 4.18) * mm, "end": v(-76.09, 3.2) * mm});
            skLineSegment(sketch, "E4.9.0.72", {"start": v(-89.09, 4.18) * mm, "end": v(-89.09, 3.2) * mm});
            skLineSegment(sketch, "E4.direction1", {"start": v(-101.36, 15.82) * mm, "end": v(-101.35, 14.42) * mm, "construction": true});
            skSolve(sketch);
        }
        {
            var Q0;
            Q0=makeQuery(id+"F0.imprint","IMPRINT",FACE,{"disambiguationData":[TD([[makeQuery(id+"F0.imprint","IMPRINT",EDGE,{"derivedFrom":sQuery(id+"F0.wireOp",EDGE,"E0.bottom")}),-1.0]])]});
            extrude(context, id + "F1", {"entities" : qUnion([Q0]), "depth" : 10 * mm});
        }
        {
            var Q0;
            Q0=makeQuery(id+"F0.imprint","IMPRINT",FACE,{"disambiguationData":[TD([[makeQuery(id+"F0.imprint","IMPRINT",EDGE,{"derivedFrom":sQuery(id+"F0.wireOp",EDGE,"E1.0")}),1.0]])]});
            extrude(context, id + "F2", {"entities" : qUnion([Q0]), "operationType" : NewBodyOperationType.ADD, "depth" : 8 * mm});
        }
        {
            var Q0;
            Q0=makeQuery(id+"F1.opExtrude","SWEPT_FACE",FACE,{"disambiguationData":[OSD([sQuery(id+"F0.wireOp",EDGE,"E0.left")])]});
            var sketch = newSketch(context, id + "F3", { "sketchPlane" : qUnion([Q0])});
            skLineSegment(sketch, "E5.bottom", {"start": v(-7.24, 0) * mm, "end": v(-12.76, 0) * mm});
            skLineSegment(sketch, "E5.left", {"start": v(-7.24, 0) * mm, "end": v(-7.24, 7) * mm});
            skLineSegment(sketch, "E5.right", {"start": v(-12.76, 0) * mm, "end": v(-12.76, 7) * mm});
            skLineSegment(sketch, "E6", {"start": v(-12.76, 7) * mm, "end": v(-10.74, 10) * mm});
            skLineSegment(sketch, "E7.MirrorCS", {"start": v(-7.24, 7) * mm, "end": v(-9.26, 10) * mm});
            skLineSegment(sketch, "E8", {"start": v(-10.74, 10) * mm, "end": v(-9.26, 10) * mm});
            skSolve(sketch);
        }
        {
            var Q0;
            Q0 = qSketchRegion(id + "F3", true);
            var Q1;
            Q1=makeQuery(id+"F3.imprint","IMPRINT",FACE,{"disambiguationData":[TD([[makeQuery(id+"F3.imprint","IMPRINT",EDGE,{"derivedFrom":sQuery(id+"F3.wireOp",EDGE,"E5.bottom")}),1.0]])]});
            extrude(context, id + "F4", {"entities" : qUnion([Q0, Q1]), "operationType" : NewBodyOperationType.ADD, "depth" : 1.8 * mm});
        }
        {
            var Q0;
            Q0=makeQuery(id+"F1.opExtrude","SWEPT_FACE",FACE,{"disambiguationData":[OSD([sQuery(id+"F0.wireOp",EDGE,"E0.right")])]});
            var sketch = newSketch(context, id + "F5", { "sketchPlane" : qUnion([Q0])});
            skLineSegment(sketch, "E9.0", {"start": v(10.74, 10) * mm, "end": v(9.26, 10) * mm});
            skLineSegment(sketch, "E9.1", {"start": v(12.76, 7) * mm, "end": v(10.74, 10) * mm});
            skLineSegment(sketch, "E9.2", {"start": v(7.24, 7) * mm, "end": v(9.26, 10) * mm});
            skLineSegment(sketch, "E9.3", {"start": v(7.24, 0) * mm, "end": v(7.24, 7) * mm});
            skLineSegment(sketch, "E9.4", {"start": v(12.76, 0) * mm, "end": v(12.76, 7) * mm});
            skLineSegment(sketch, "E9.5", {"start": v(7.24, 0) * mm, "end": v(12.76, 0) * mm});
            skSolve(sketch);
        }
        {
            var Q0;
            Q0=makeQuery(id+"F5.imprint","IMPRINT",FACE,{"disambiguationData":[TD([[makeQuery(id+"F5.imprint","IMPRINT",EDGE,{"derivedFrom":sQuery(id+"F5.wireOp",EDGE,"E9.0")}),1.0]])]});
            extrude(context, id + "F6", {"entities" : qUnion([Q0]), "operationType" : NewBodyOperationType.ADD, "depth" : 1.8 * mm});
        }
        {
            var Q0;
            Q0=makeQuery(id+"F1.opExtrude","CAP_EDGE",EDGE,{"disambiguationData":[OSD([sQuery(id+"F0.wireOp",EDGE,"E1.0")])],"isStart":false});
            var Q1;
            Q1=makeQuery(id+"F1.opExtrude","CAP_EDGE",EDGE,{"disambiguationData":[OSD([sQuery(id+"F0.wireOp",EDGE,"E1.1")])],"isStart":false});
            var Q2;
            Q2=makeQuery(id+"F1.opExtrude","CAP_EDGE",EDGE,{"disambiguationData":[OSD([sQuery(id+"F0.wireOp",EDGE,"E1.2")])],"isStart":false});
            var Q3;
            Q3=makeQuery(id+"F1.opExtrude","CAP_EDGE",EDGE,{"disambiguationData":[OSD([sQuery(id+"F0.wireOp",EDGE,"E1.3")])],"isStart":false});
            chamfer(context, id + "F7", {"entities" : qUnion([Q0, Q1, Q2, Q3]), "width" : .5 * mm, "tangentPropagation" : true});
        }
    });
